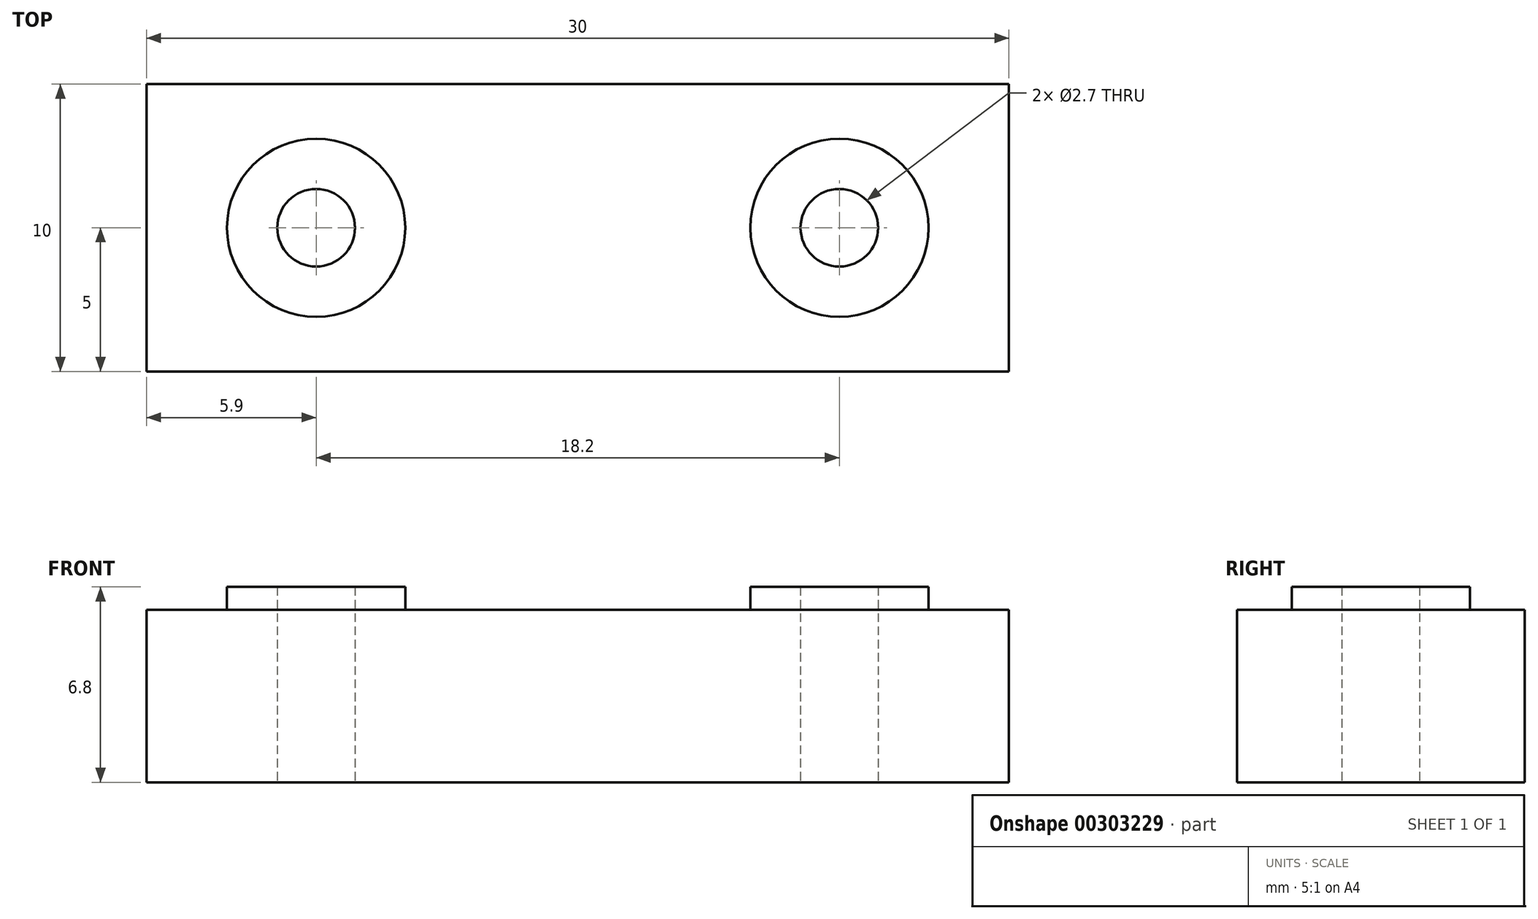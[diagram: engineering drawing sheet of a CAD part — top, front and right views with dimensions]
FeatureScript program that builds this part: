
annotation { "Feature Type Name" : "Feature", "Feature Type Description" : "" }
export const myFeature = defineFeature(function(context is Context, id is Id, definition is map)
    precondition{}
    {
        {
            var Q0;
            Q0=qCreatedBy(makeId("Top.planeOp"),FACE);
            var sketch = newSketch(context, id + "F0", { "sketchPlane" : qUnion([Q0])});
            skLineSegment(sketch, "E0.bottom", {"start": v(-15, 5) * mm, "end": v(15, 5) * mm});
            skLineSegment(sketch, "E0.top", {"start": v(-15, -5) * mm, "end": v(15, -5) * mm});
            skLineSegment(sketch, "E0.left", {"start": v(-15, 5) * mm, "end": v(-15, -5) * mm});
            skLineSegment(sketch, "E0.right", {"start": v(15, 5) * mm, "end": v(15, -5) * mm});
            skCircle(sketch, "E1", {"center": v(-9.1, 0) * mm, "radius": 1.35 * mm});
            skCircle(sketch, "E2", {"center": v(9.1, 0) * mm, "radius": 1.35 * mm});
            skSolve(sketch);
        }
        {
            var Q0;
            Q0 = qSketchRegion(id + "F0", true);
            extrude(context, id + "F1", {"entities" : qUnion([Q0]), "depth" : 6 * mm});
        }
        {
            var Q0;
            Q0=makeQuery(id+"F1.opExtrude","CAP_FACE",FACE,{"disambiguationData":[OSD([sQuery(id+"F0.wireOp",EDGE,"E0.bottom"),sQuery(id+"F0.wireOp",EDGE,"E0.top"),sQuery(id+"F0.wireOp",EDGE,"E0.left"),sQuery(id+"F0.wireOp",EDGE,"E0.right"),sQuery(id+"F0.wireOp",EDGE,"E1"),sQuery(id+"F0.wireOp",EDGE,"E2")])],"isStart":false});
            var sketch = newSketch(context, id + "F2", { "sketchPlane" : qUnion([Q0])});
            skCircle(sketch, "E3", {"center": v(-9.1, 0) * mm, "radius": 1.35 * mm});
            skCircle(sketch, "E4", {"center": v(9.1, 0) * mm, "radius": 1.35 * mm});
            skCircle(sketch, "E5", {"center": v(-9.1, 0) * mm, "radius": 3.1 * mm});
            skCircle(sketch, "E6", {"center": v(9.1, 0) * mm, "radius": 3.1 * mm});
            skSolve(sketch);
        }
        {
            var Q0;
            Q0 = qSketchRegion(id + "F2", true);
            extrude(context, id + "F3", {"entities" : qUnion([Q0]), "operationType" : NewBodyOperationType.ADD, "depth" : 0.8 * mm});
        }
    });
